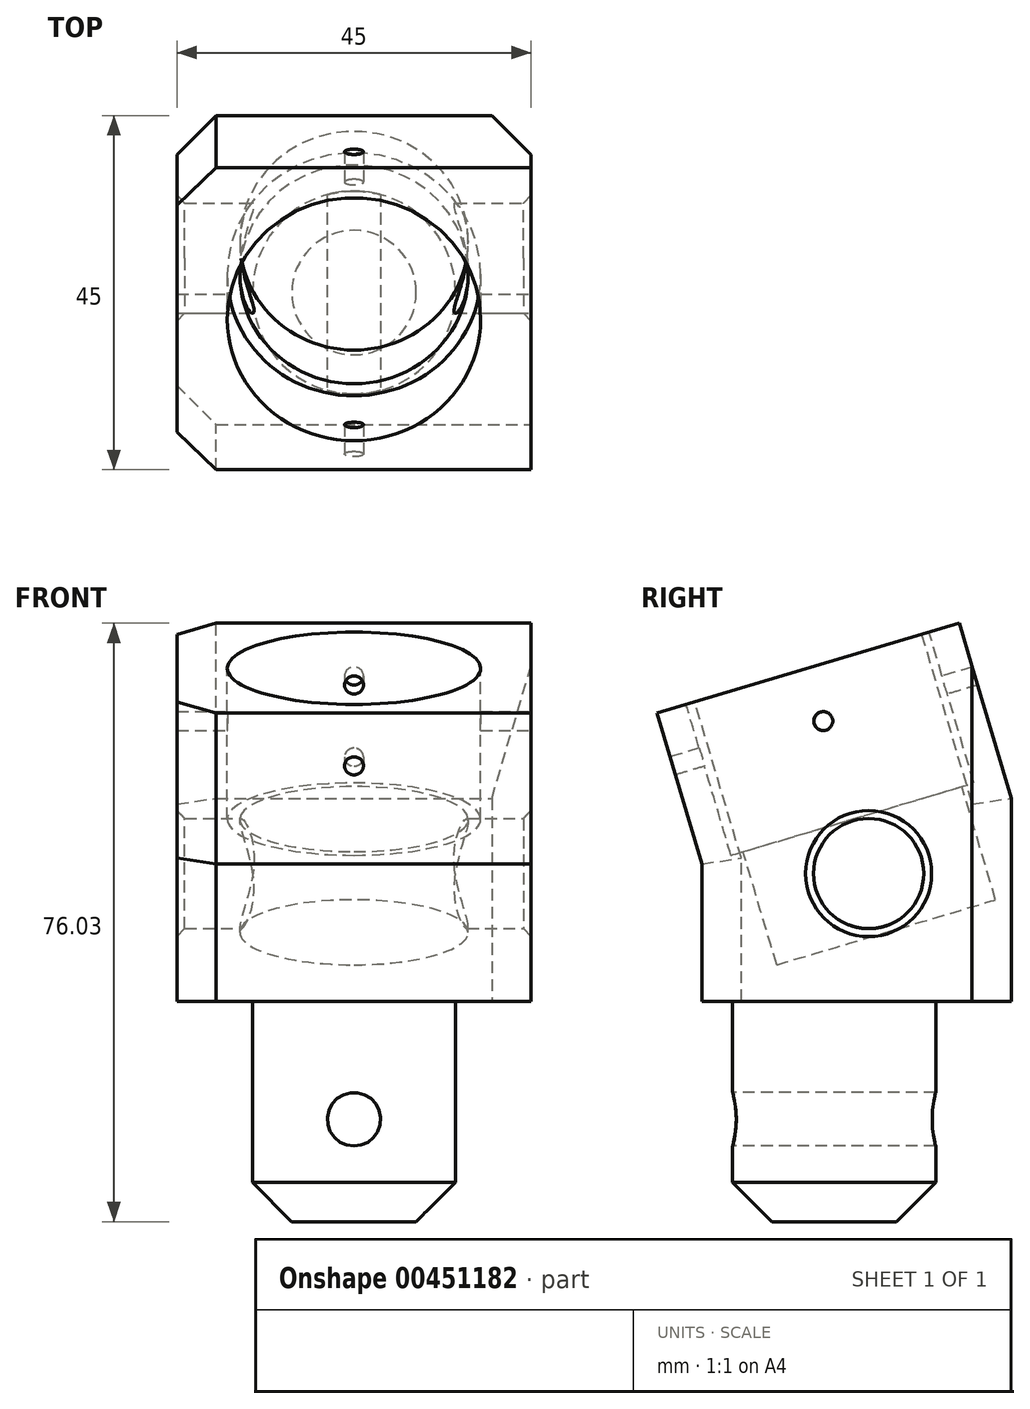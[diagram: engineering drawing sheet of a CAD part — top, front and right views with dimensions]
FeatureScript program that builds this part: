
annotation { "Feature Type Name" : "Feature", "Feature Type Description" : "" }
export const myFeature = defineFeature(function(context is Context, id is Id, definition is map)
    precondition{}
    {
        {
            var Q0;
            Q0=qCreatedBy(makeId("Top.planeOp"),FACE);
            var sketch = newSketch(context, id + "F0", { "sketchPlane" : qUnion([Q0])});
            skCircle(sketch, "E0", {"center": v(0, 0) * mm, "radius": 12.9 * mm});
            skSolve(sketch);
        }
        {
            var Q0;
            Q0=qSketchRegion(id+"F0",true);
            extrude(context, id + "F1", {"entities" : qUnion([Q0]), "depth" : 28 * mm, "offsetDistance" : 25 * mm});
        }
        {
            var Q0;
            Q0=makeQuery(id+"F1.opExtrude","CAP_FACE",FACE,{"disambiguationData":[OSD([sQuery(id+"F0.wireOp",EDGE,"E0"),sQuery(id+"F0.wireOp",EDGE,"SnAVlE3f-jAuu-pCCq-HaNH-xM0daaBw2DbN")])],"isStart":false});
            var sketch = newSketch(context, id + "F2", { "sketchPlane" : qUnion([Q0])});
            skCircle(sketch, "E1", {"center": v(0, 0) * mm, "radius": 19 * mm, "construction": true});
            skLineSegment(sketch, "E2.bottom", {"start": v(22.5, -22.5) * mm, "end": v(-22.5, -22.5) * mm});
            skLineSegment(sketch, "E2.top", {"start": v(22.5, 22.5) * mm, "end": v(-22.5, 22.5) * mm});
            skLineSegment(sketch, "E2.left", {"start": v(22.5, -22.5) * mm, "end": v(22.5, 22.5) * mm});
            skLineSegment(sketch, "E2.right", {"start": v(-22.5, -22.5) * mm, "end": v(-22.5, 22.5) * mm});
            skSolve(sketch);
        }
        {
            var Q0;
            Q0=qSketchRegion(id+"F2",true);
            extrude(context, id + "F3", {"entities" : qUnion([Q0]), "operationType" : NewBodyOperationType.ADD, "depth" : 50 * mm, "offsetDistance" : 25 * mm});
        }
        {
            var Q0;
            Q0=makeQuery(id+"F3.opExtrude","SWEPT_FACE",FACE,{"disambiguationData":[OSD([sQuery(id+"F2.wireOp",EDGE,"E2.left")])]});
            var sketch = newSketch(context, id + "F4", { "sketchPlane" : qUnion([Q0])});
            skLineSegment(sketch, "E3", {"start": v(-22.5, 64.62) * mm, "end": v(-22.5, 78) * mm});
            skLineSegment(sketch, "E4", {"start": v(-22.5, 78) * mm, "end": v(-22.5, 78) * mm});
            skLineSegment(sketch, "E5", {"start": v(-22.5, 64.62) * mm, "end": v(22.5, 78) * mm});
            skLineSegment(sketch, "E6", {"start": v(22.5, 78) * mm, "end": v(-22.5, 78) * mm});
            skSolve(sketch);
        }
        {
            var Q0;
            Q0 = qSketchRegion(id + "F4", true);
            extrude(context, id + "F5", {"entities" : qUnion([Q0]), "operationType" : NewBodyOperationType.REMOVE, "endBound" : BoundingType.THROUGH_ALL, "oppositeDirection" : true, "depth" : 25 * mm, "offsetDistance" : 25 * mm});
        }
        {
            var Q0;
            Q0=makeQuery(id+"F5.boolean.opBoolean","COPY",FACE,{"derivedFrom":makeQuery(id+"F5.opExtrude","SWEPT_FACE",FACE,{"disambiguationData":[OSD([sQuery(id+"F4.wireOp",EDGE,"E5")])]})});
            var sketch = newSketch(context, id + "F6", { "sketchPlane" : qUnion([Q0])});
            skCircle(sketch, "E7", {"center": v(0, 16.8) * mm, "radius": 14.5 * mm});
            skSolve(sketch);
        }
        {
            var Q0;
            Q0 = qSketchRegion(id + "F6", true);
            extrude(context, id + "F7", {"entities" : qUnion([Q0]), "operationType" : NewBodyOperationType.REMOVE, "oppositeDirection" : true, "depth" : 35 * mm, "offsetDistance" : 25 * mm});
        }
        {
            var Q0;
            Q0=makeQuery(id+"F5.boolean.opBoolean","COPY",FACE,{"derivedFrom":makeQuery(id+"F5.opExtrude","SWEPT_FACE",FACE,{"disambiguationData":[OSD([sQuery(id+"F4.wireOp",EDGE,"E5")])]})});
            var sketch = newSketch(context, id + "F8", { "sketchPlane" : qUnion([Q0])});
            skCircle(sketch, "E8", {"center": v(0, 16.8) * mm, "radius": 16.1 * mm});
            skSolve(sketch);
        }
        {
            var Q0;
            Q0 = qSketchRegion(id + "F8", true);
            extrude(context, id + "F9", {"entities" : qUnion([Q0]), "operationType" : NewBodyOperationType.REMOVE, "oppositeDirection" : true, "depth" : 20 * mm, "offsetDistance" : 25 * mm});
        }
        {
            var Q0;
            Q0=qCreatedBy(makeId("Front.planeOp"),FACE);
            var sketch = newSketch(context, id + "F10", { "sketchPlane" : qUnion([Q0])});
            skCircle(sketch, "E9", {"center": v(0, 13) * mm, "radius": 3.4 * mm});
            skSolve(sketch);
        }
        {
            var Q0;
            Q0 = qSketchRegion(id + "F10", true);
            extrude(context, id + "F11", {"entities" : qUnion([Q0]), "operationType" : NewBodyOperationType.REMOVE, "oppositeDirection" : true, "depth" : 65.6 * mm, "offsetDistance" : 25 * mm, "symmetric" : true});
        }
        {
            var Q0;
            Q0=qCreatedBy(makeId("Right.planeOp"),FACE);
            var sketch = newSketch(context, id + "F12", { "sketchPlane" : qUnion([Q0])});
            skCircle(sketch, "E10", {"center": v(-1.39, 63.6) * mm, "radius": 1.2 * mm});
            skLineSegment(sketch, "E11.0", {"start": v(-18.81, 65.72) * mm, "end": v(12.05, 74.9) * mm});
            skLineSegment(sketch, "E12", {"start": v(-3.38, 70.3) * mm, "end": v(5.56, 40.22) * mm, "construction": true});
            skCircle(sketch, "E13", {"center": v(4.37, 44.22) * mm, "radius": 7 * mm});
            skSolve(sketch);
        }
        {
            var Q0;
            Q0 = qSketchRegion(id + "F12", true);
            extrude(context, id + "F13", {"entities" : qUnion([Q0]), "operationType" : NewBodyOperationType.REMOVE, "oppositeDirection" : true, "depth" : 130.4 * mm, "offsetDistance" : 25 * mm, "symmetric" : true});
        }
        {
            var Q0;
            Q0=makeQuery(id+"F3.opExtrude","SWEPT_FACE",FACE,{"disambiguationData":[OSD([sQuery(id+"F2.wireOp",EDGE,"E2.left")])]});
            var sketch = newSketch(context, id + "F14", { "sketchPlane" : qUnion([Q0])});
            skLineSegment(sketch, "E14", {"start": v(-22.5, 64.62) * mm, "end": v(-16.8, 45.45) * mm});
            skLineSegment(sketch, "E15", {"start": v(15.89, 76.03) * mm, "end": v(22.5, 53.79) * mm});
            skLineSegment(sketch, "E16", {"start": v(22.5, 53.79) * mm, "end": v(22.5, 78) * mm});
            skLineSegment(sketch, "E17", {"start": v(22.5, 78) * mm, "end": v(15.89, 76.03) * mm});
            skLineSegment(sketch, "E18", {"start": v(-16.8, 45.45) * mm, "end": v(-22.5, 43.76) * mm});
            skLineSegment(sketch, "E19", {"start": v(-22.5, 43.76) * mm, "end": v(-22.5, 64.62) * mm});
            skLineSegment(sketch, "E20.0", {"start": v(-18.81, 65.72) * mm, "end": v(12.05, 74.9) * mm});
            skLineSegment(sketch, "E21", {"start": v(-16.8, 45.45) * mm, "end": v(-16.8, 28) * mm});
            skLineSegment(sketch, "E22", {"start": v(-16.8, 28) * mm, "end": v(-22.5, 28) * mm});
            skLineSegment(sketch, "E23", {"start": v(-22.5, 28) * mm, "end": v(-22.5, 43.76) * mm});
            skSolve(sketch);
        }
        {
            var Q0;
            Q0 = qSketchRegion(id + "F14", true);
            extrude(context, id + "F15", {"entities" : qUnion([Q0]), "operationType" : NewBodyOperationType.REMOVE, "endBound" : BoundingType.THROUGH_ALL, "oppositeDirection" : true, "depth" : 25 * mm, "offsetDistance" : 25 * mm});
        }
        {
            var Q0;
            Q0=makeQuery(id+"F15.boolean.opBoolean","COPY",FACE,{"derivedFrom":makeQuery(id+"F15.opExtrude","SWEPT_FACE",FACE,{"disambiguationData":[OSD([sQuery(id+"F14.wireOp",EDGE,"E14")])]})});
            var sketch = newSketch(context, id + "F16", { "sketchPlane" : qUnion([Q0])});
            skCircle(sketch, "E24", {"center": v(0, 61.35) * mm, "radius": 1.2 * mm});
            skSolve(sketch);
        }
        {
            var Q0;
            Q0 = qSketchRegion(id + "F16", true);
            extrude(context, id + "F17", {"entities" : qUnion([Q0]), "operationType" : NewBodyOperationType.REMOVE, "endBound" : BoundingType.THROUGH_ALL, "oppositeDirection" : true, "depth" : 25 * mm, "offsetDistance" : 25 * mm});
        }
        {
            var Q0;
            Q0=makeQuery(id+"F15.boolean.opBoolean","COPY",EDGE,{"derivedFrom":makeQuery(id+"F15.opExtrude","CAP_EDGE",EDGE,{"disambiguationData":[OSD([sQuery(id+"F14.wireOp",EDGE,"E14")])],"isStart":true})});
            var Q1;
            Q1=makeQuery(id+"F15.boolean.opBoolean","COPY",EDGE,{"derivedFrom":makeQuery(id+"F15.opExtrude","CAP_EDGE",EDGE,{"disambiguationData":[OSD([sQuery(id+"F14.wireOp",EDGE,"E21")])],"isStart":true})});
            var Q2;
            Q2=makeQuery(id+"F15.boolean.opBoolean","COPY",EDGE,{"derivedFrom":makeQuery(id+"F15.opExtrude","CAP_EDGE",EDGE,{"disambiguationData":[OSD([sQuery(id+"F14.wireOp",EDGE,"E15")])],"isStart":true})});
            var Q3;
            Q3=makeQuery(id+"F3.opExtrude","SWEPT_EDGE",EDGE,{"disambiguationData":[OSD([sQuery(id+"F2.wireOp",EDGE,"E2.top"),sQuery(id+"F2.wireOp",EDGE,"E2.left")])]});
            var Q4;
            Q4=makeQuery(id+"F3.opExtrude","SWEPT_EDGE",EDGE,{"disambiguationData":[OSD([sQuery(id+"F2.wireOp",EDGE,"E2.top"),sQuery(id+"F2.wireOp",EDGE,"E2.right")])]});
            var Q5;
            Q5=makeQuery(id+"F15.boolean.opBoolean","INTERSECT",EDGE,{"derivedFrom":[makeQuery(id+"F3.opExtrude","SWEPT_FACE",FACE,{"disambiguationData":[OSD([sQuery(id+"F2.wireOp",EDGE,"E2.right")])]}),makeQuery(id+"F15.opExtrude","SWEPT_FACE",FACE,{"disambiguationData":[OSD([sQuery(id+"F14.wireOp",EDGE,"E15")])]})]});
            var Q6;
            Q6=makeQuery(id+"F15.boolean.opBoolean","INTERSECT",EDGE,{"derivedFrom":[makeQuery(id+"F3.opExtrude","SWEPT_FACE",FACE,{"disambiguationData":[OSD([sQuery(id+"F2.wireOp",EDGE,"E2.right")])]}),makeQuery(id+"F15.opExtrude","SWEPT_FACE",FACE,{"disambiguationData":[OSD([sQuery(id+"F14.wireOp",EDGE,"E14")])]})]});
            var Q7;
            Q7=makeQuery(id+"F15.boolean.opBoolean","INTERSECT",EDGE,{"derivedFrom":[makeQuery(id+"F3.opExtrude","SWEPT_FACE",FACE,{"disambiguationData":[OSD([sQuery(id+"F2.wireOp",EDGE,"E2.right")])]}),makeQuery(id+"F15.opExtrude","SWEPT_FACE",FACE,{"disambiguationData":[OSD([sQuery(id+"F14.wireOp",EDGE,"E21")])]})]});
            var Q8;
            Q8=makeQuery(id+"F1.opExtrude","CAP_EDGE",EDGE,{"disambiguationData":[OSD([sQuery(id+"F0.wireOp",EDGE,"E0")])],"isStart":true});
            chamfer(context, id + "F18", {"entities" : qUnion([Q0, Q1, Q2, Q3, Q4, Q5, Q6, Q7, Q8]), "width" : 5 * mm, "tangentPropagation" : true});
        }
        {
            var Q0;
            Q0=makeQuery(id+"F9.boolean.opBoolean","COPY",EDGE,{"derivedFrom":makeQuery(id+"F9.opExtrude","CAP_EDGE",EDGE,{"disambiguationData":[OSD([sQuery(id+"F8.wireOp",EDGE,"E8")])],"isStart":true})});
            var Q1;
            Q1=makeQuery(id+"F13.boolean.opBoolean","INTERSECT",EDGE,{"derivedFrom":[makeQuery(id+"F3.opExtrude","SWEPT_FACE",FACE,{"disambiguationData":[OSD([sQuery(id+"F2.wireOp",EDGE,"E2.left")])]}),makeQuery(id+"F13.opExtrude","SWEPT_FACE",FACE,{"disambiguationData":[OSD([sQuery(id+"F12.wireOp",EDGE,"E13")])]})]});
            var Q2;
            Q2=makeQuery(id+"F13.boolean.opBoolean","INTERSECT",EDGE,{"derivedFrom":[makeQuery(id+"F3.opExtrude","SWEPT_FACE",FACE,{"disambiguationData":[OSD([sQuery(id+"F2.wireOp",EDGE,"E2.right")])]}),makeQuery(id+"F13.opExtrude","SWEPT_FACE",FACE,{"disambiguationData":[OSD([sQuery(id+"F12.wireOp",EDGE,"E13")])]})]});
            chamfer(context, id + "F19", {"entities" : qUnion([Q0, Q1, Q2]), "width" : 1 * mm, "tangentPropagation" : true});
        }
    });
